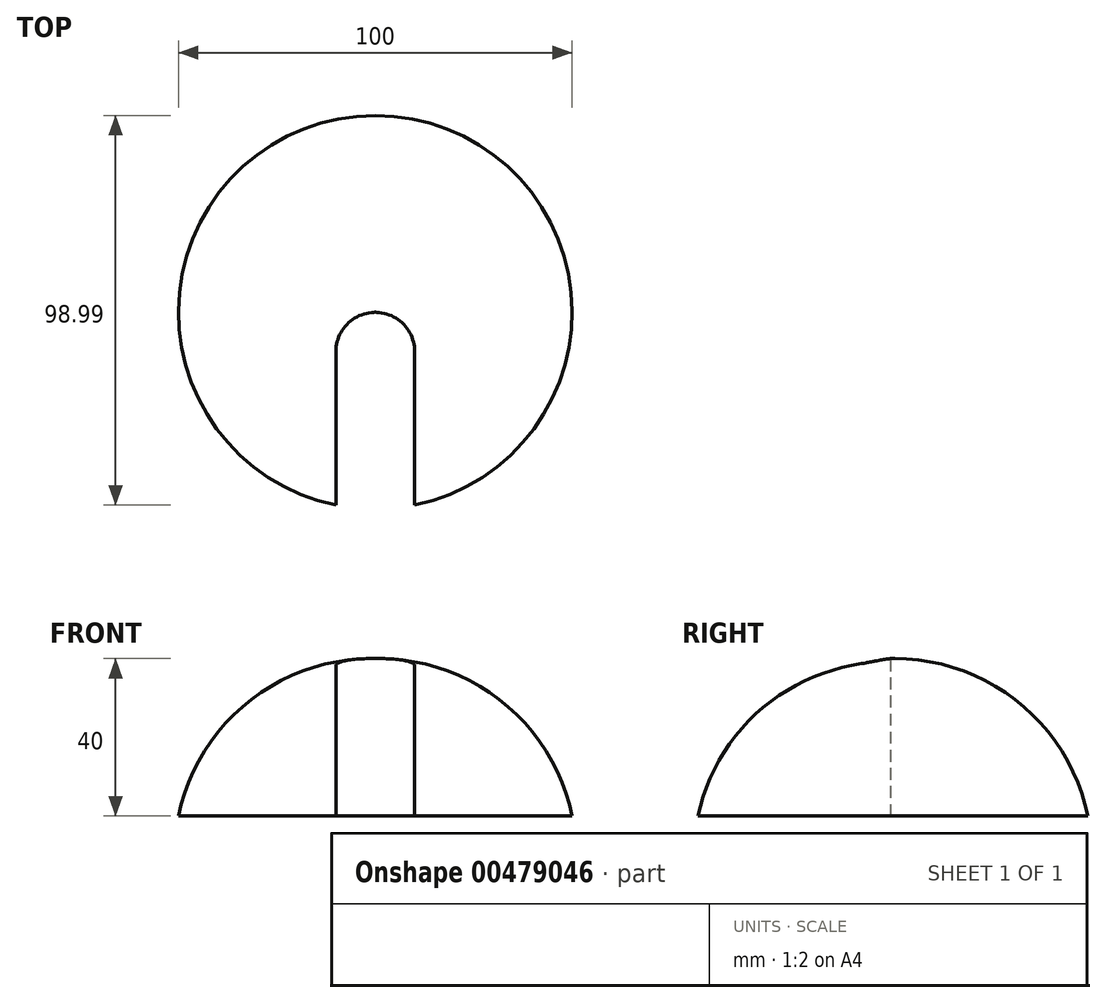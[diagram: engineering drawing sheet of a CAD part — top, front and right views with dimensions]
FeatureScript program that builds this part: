
annotation { "Feature Type Name" : "Feature", "Feature Type Description" : "" }
export const myFeature = defineFeature(function(context is Context, id is Id, definition is map)
    precondition{}
    {
        {
            var Q0;
            Q0=qCreatedBy(makeId("Top.planeOp"),FACE);
            var sketch = newSketch(context, id + "F0", { "sketchPlane" : qUnion([Q0])});
            skCircle(sketch, "E0", {"center": v(0, 0) * mm, "radius": 50 * mm});
            skSolve(sketch);
        }
        {
            var Q0;
            Q0 = qSketchRegion(id + "F0", true);
            extrude(context, id + "F1", {"entities" : qUnion([Q0]), "depth" : 40 * mm});
        }
        {
            var Q0;
            Q0=makeQuery(id+"F1.opExtrude","CAP_FACE",FACE,{"disambiguationData":[OSD([sQuery(id+"F0.wireOp",EDGE,"E0")])],"isStart":false});
            fillet(context, id + "F2", {"entities" : qUnion([Q0]), "radius" : 50 * mm, "allowEdgeOverflow" : false});
        }
        {
            var Q0;
            Q0=qCreatedBy(makeId("Right.planeOp"),FACE);
            var sketch = newSketch(context, id + "F3", { "sketchPlane" : qUnion([Q0])});
            skLineSegment(sketch, "E1", {"start": v(0, 0) * mm, "end": v(-50, 0) * mm});
            skLineSegment(sketch, "E2", {"start": v(0, 0) * mm, "end": v(0, 40) * mm});
            skArc(sketch, "E3", {"start": v(0, 40) * mm, "mid": v(-32.24, 29.05) * mm, "end": v(-50, 0) * mm});
            skArc(sketch, "E4.0", {"start": v(-0.15, 32.5) * mm, "mid": v(-26.95, 23.67) * mm, "end": v(-42.32, 0) * mm});
            skLineSegment(sketch, "E5", {"start": v(-50, 0) * mm, "end": v(-42.32, 0) * mm});
            skSolve(sketch);
        }
        {
            var Q0;
            Q0 = qSketchRegion(id + "F3", true);
            extrude(context, id + "F4", {"entities" : qUnion([Q0]), "operationType" : NewBodyOperationType.REMOVE, "oppositeDirection" : true, "depth" : 10 * mm, "hasSecondDirection" : true, "secondDirectionOppositeDirection" : false, "secondDirectionDepth" : 10 * mm});
        }
        {
            var Q0;
            Q0=makeQuery(id+"F4.boolean.opBoolean","COPY",EDGE,{"derivedFrom":makeQuery(id+"F4.opExtrude","CAP_EDGE",EDGE,{"disambiguationData":[OSD([sQuery(id+"F3.wireOp",EDGE,"E2")])],"isStart":false})});
            var Q1;
            Q1=makeQuery(id+"F4.boolean.opBoolean","COPY",EDGE,{"derivedFrom":makeQuery(id+"F4.opExtrude","CAP_EDGE",EDGE,{"disambiguationData":[OSD([sQuery(id+"F3.wireOp",EDGE,"E2")])],"isStart":true})});
            fillet(context, id + "F5", {"entities" : qUnion([Q0, Q1]), "radius" : 10 * mm, "tangentPropagation" : true, "allowEdgeOverflow" : false});
        }
    });
